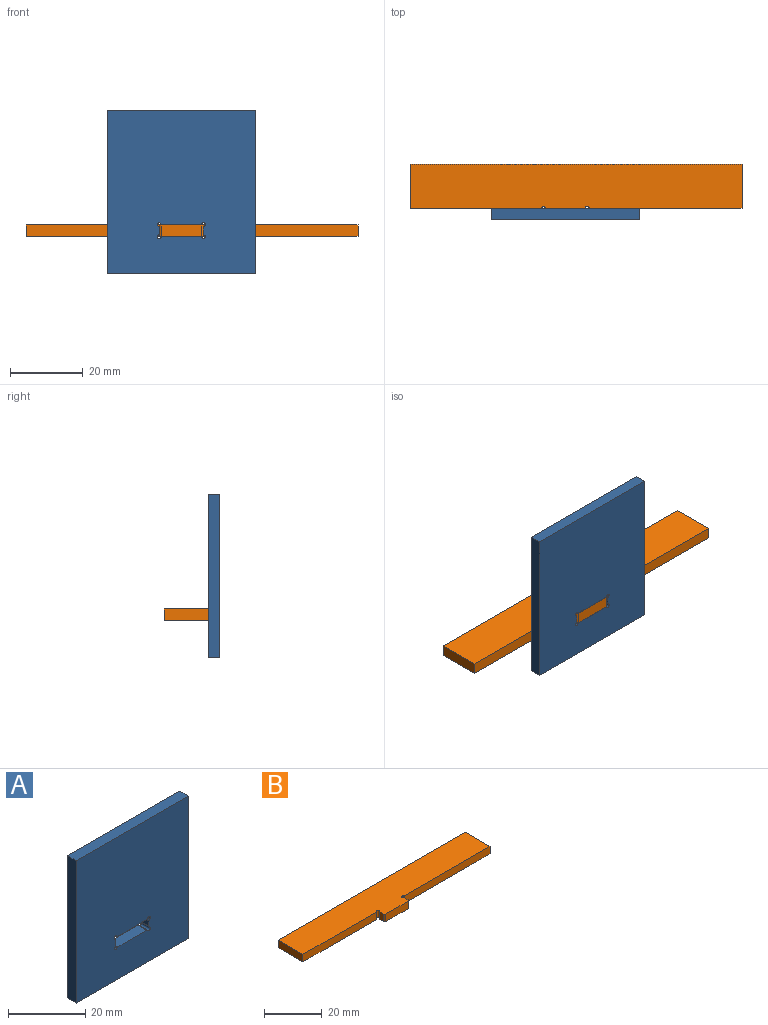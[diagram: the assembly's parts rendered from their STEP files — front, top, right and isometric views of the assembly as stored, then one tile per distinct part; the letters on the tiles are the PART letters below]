
ASSEMBLY  parts=2 mates=1
PART A: 21 faces, bbox 40.9x3.2x45 mm
  f0: plane 3.18x2.01mm, normal (1,0,0), area 6.4mm2, adj f8,f9,f12,f19
  f1: plane 10.47x3.18mm, normal (0,0,-1), area 33.2mm2, adj f8,f9,f16,f17
  f2: plane 3.18x1.64mm, normal (-1,0,0), area 5.2mm2, adj f8,f9,f14,f18
  f3: plane 10.47x3.18mm, normal (0,0,1), area 33.2mm2, adj f8,f9,f15,f20
  f4: plane 40.94x3.18mm, normal (0,0,1), area 130mm2, adj f5,f7,f8,f9
  f5: plane 45x3.18mm, normal (-1,0,0), area 142.9mm2, adj f4,f6,f8,f9
  f6: plane 40.94x3.18mm, normal (0,0,-1), area 130mm2, adj f5,f7,f8,f9
  f7: plane 45x3.18mm, normal (1,0,0), area 142.9mm2, adj f4,f6,f8,f9
  f8: plane 45x40.94mm, normal (0,-1,0), area 1798.6mm2, adj f0,f1,f2,f3,f4,f5,f6,f7
  f9: plane 45x40.94mm, normal (0,1,0), area 1798.6mm2, adj f0,f1,f2,f3,f4,f5,f6,f7
  f10: cylinder r=0.5mm len=3.18mm, axis (0,1,0), area 5.8mm2, adj f8,f9,f19,f20
  f11: cylinder r=0.5mm len=3.18mm, axis (0,1,0), area 5.8mm2, adj f8,f9,f17,f18
  f12: cylinder r=0.5mm len=3.18mm, axis (0,1,0), area 6.6mm2, adj f0,f8,f9,f16
  f13: cylinder r=0.5mm len=3.18mm, axis (0,1,0), area 5.8mm2, adj f8,f9,f14,f15
  f14: cylinder r=0.5mm len=3.18mm, axis (0,1,0), area 1.7mm2, adj f2,f8,f9,f13
  f15: cylinder r=0.5mm len=3.18mm, axis (0,1,0), area 1.7mm2, adj f3,f8,f9,f13
  f16: cylinder r=0.5mm len=3.18mm, axis (0,1,0), area 1.7mm2, adj f1,f8,f9,f12
  f17: cylinder r=0.5mm len=3.18mm, axis (0,1,0), area 1.7mm2, adj f1,f8,f9,f11
  f18: cylinder r=0.5mm len=3.18mm, axis (0,1,0), area 1.7mm2, adj f2,f8,f9,f11
  f19: cylinder r=0.5mm len=3.18mm, axis (0,1,0), area 1.7mm2, adj f0,f8,f9,f10
  f20: cylinder r=0.5mm len=3.18mm, axis (0,1,0), area 1.7mm2, adj f3,f8,f9,f10
PART B: 18 faces, bbox 91.3x15.3x3.2 mm
  f0: plane 35.85x3.18mm, normal (0,-1,0), area 113.8mm2, adj f7,f8,f9,f12
  f1: plane 3.18x1.81mm, normal (-1,0,0), area 5.7mm2, adj f8,f9,f13,f16
  f2: plane 3.18x1.81mm, normal (1,0,0), area 5.7mm2, adj f8,f9,f14,f17
  f3: plane 41.74x3.18mm, normal (0,-1,0), area 132.5mm2, adj f5,f8,f9,f15
  f4: plane 11x3.18mm, normal (0,-1,0), area 34.9mm2, adj f8,f9,f16,f17
  f5: plane 12.15x3.18mm, normal (1,0,0), area 38.6mm2, adj f3,f6,f8,f9
  f6: plane 91.33x3.18mm, normal (0,1,0), area 290mm2, adj f5,f7,f8,f9
  f7: plane 12.15x3.18mm, normal (-1,0,0), area 38.6mm2, adj f0,f6,f8,f9
  f8: plane 91.33x15.33mm, normal (0,0,1), area 1146.4mm2, adj f0,f1,f2,f3,f4,f5,f6,f7
  f9: plane 91.33x15.33mm, normal (0,0,-1), area 1146.4mm2, adj f0,f1,f2,f3,f4,f5,f6,f7
  f10: cylinder r=0.5mm len=3.18mm, axis (0,0,-1), area 5.8mm2, adj f8,f9,f14,f15
  f11: cylinder r=0.5mm len=3.18mm, axis (0,0,-1), area 5.8mm2, adj f8,f9,f12,f13
  f12: cylinder r=0.5mm len=3.18mm, axis (0,0,-1), area 1.7mm2, adj f0,f8,f9,f11
  f13: cylinder r=0.5mm len=3.18mm, axis (0,0,-1), area 1.7mm2, adj f1,f8,f9,f11
  f14: cylinder r=0.5mm len=3.18mm, axis (0,0,-1), area 1.7mm2, adj f2,f8,f9,f10
  f15: cylinder r=0.5mm len=3.18mm, axis (0,0,-1), area 1.7mm2, adj f3,f8,f9,f10
  f16: cylinder r=0.5mm len=3.18mm, axis (0,0,-1), area 2.5mm2, adj f1,f4,f8,f9
  f17: cylinder r=0.5mm len=3.18mm, axis (0,0,1), area 2.5mm2, adj f2,f4,f8,f9
PLACE A t=(-20.54,38.13,18.04)mm
PLACE B t=(-20.44,38.13,16.45)mm
MATE fastened A.f8 <-> B.f4  axis (0,-1,0) through (-20.44,34.96,19.72)mm
